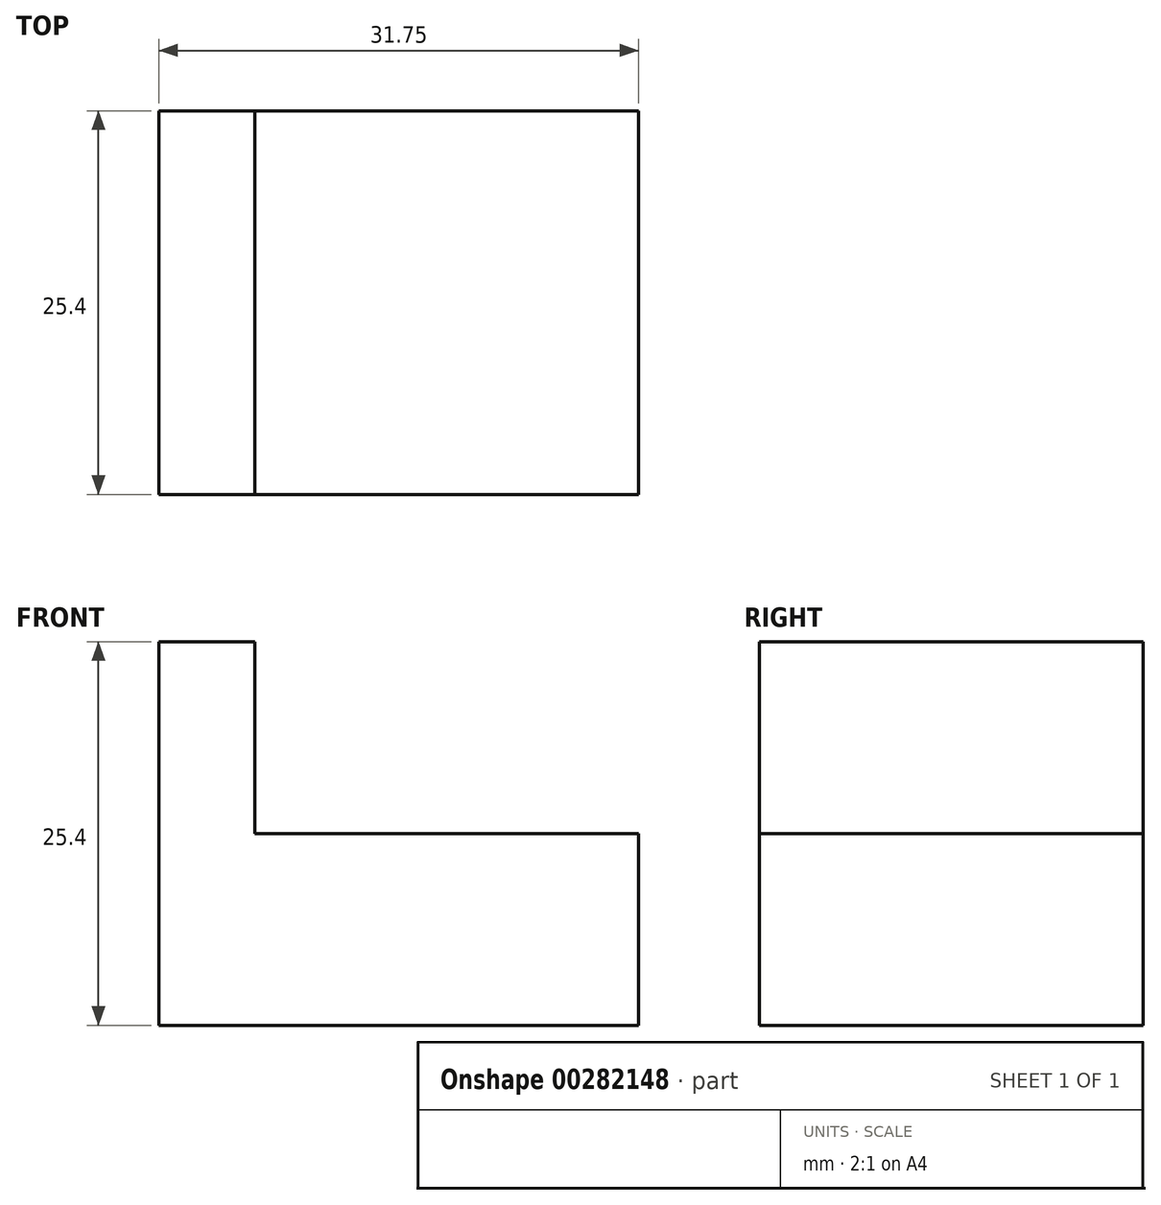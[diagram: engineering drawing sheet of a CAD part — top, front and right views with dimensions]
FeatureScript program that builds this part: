
annotation { "Feature Type Name" : "Feature", "Feature Type Description" : "" }
export const myFeature = defineFeature(function(context is Context, id is Id, definition is map)
    precondition{}
    {
        {
            var Q0;
            Q0=qCreatedBy(makeId("Front.planeOp"),FACE);
            var sketch = newSketch(context, id + "F0", { "sketchPlane" : qUnion([Q0])});
            skLineSegment(sketch, "E0", {"start": v(0, 0) * mm, "end": v(31.75, 0) * mm});
            skLineSegment(sketch, "E1", {"start": v(31.75, 0) * mm, "end": v(31.75, 12.7) * mm});
            skLineSegment(sketch, "E2", {"start": v(31.75, 12.7) * mm, "end": v(0, 12.7) * mm});
            skLineSegment(sketch, "E3", {"start": v(0, 12.7) * mm, "end": v(0, 0) * mm});
            skSolve(sketch);
        }
        {
            var Q0;
            Q0=makeQuery(id+"F0.imprint","IMPRINT",FACE,{"disambiguationData":[TD([[makeQuery(id+"F0.imprint","IMPRINT",EDGE,{"derivedFrom":sQuery(id+"F0.wireOp",EDGE,"E0")}),1.0]])]});
            extrude(context, id + "F1", {"entities" : qUnion([Q0]), "depth" : 25.4 * mm});
        }
        {
            var Q0;
            Q0=qCreatedBy(makeId("Front.planeOp"),FACE);
            var sketch = newSketch(context, id + "F2", { "sketchPlane" : qUnion([Q0])});
            skLineSegment(sketch, "E4", {"start": v(0, 0) * mm, "end": v(0, 25.4) * mm});
            skLineSegment(sketch, "E5", {"start": v(0, 25.4) * mm, "end": v(6.35, 25.4) * mm});
            skLineSegment(sketch, "E6", {"start": v(6.35, 25.4) * mm, "end": v(6.35, 0) * mm});
            skLineSegment(sketch, "E7", {"start": v(6.35, 0) * mm, "end": v(0, 0) * mm});
            skSolve(sketch);
        }
        {
            var Q0;
            Q0=makeQuery(id+"F2.imprint","IMPRINT",FACE,{"disambiguationData":[TD([[makeQuery(id+"F2.imprint","IMPRINT",EDGE,{"derivedFrom":sQuery(id+"F2.wireOp",EDGE,"E4")}),-1.0]])]});
            extrude(context, id + "F3", {"entities" : qUnion([Q0]), "operationType" : NewBodyOperationType.ADD, "depth" : 25.4 * mm});
        }
    });
